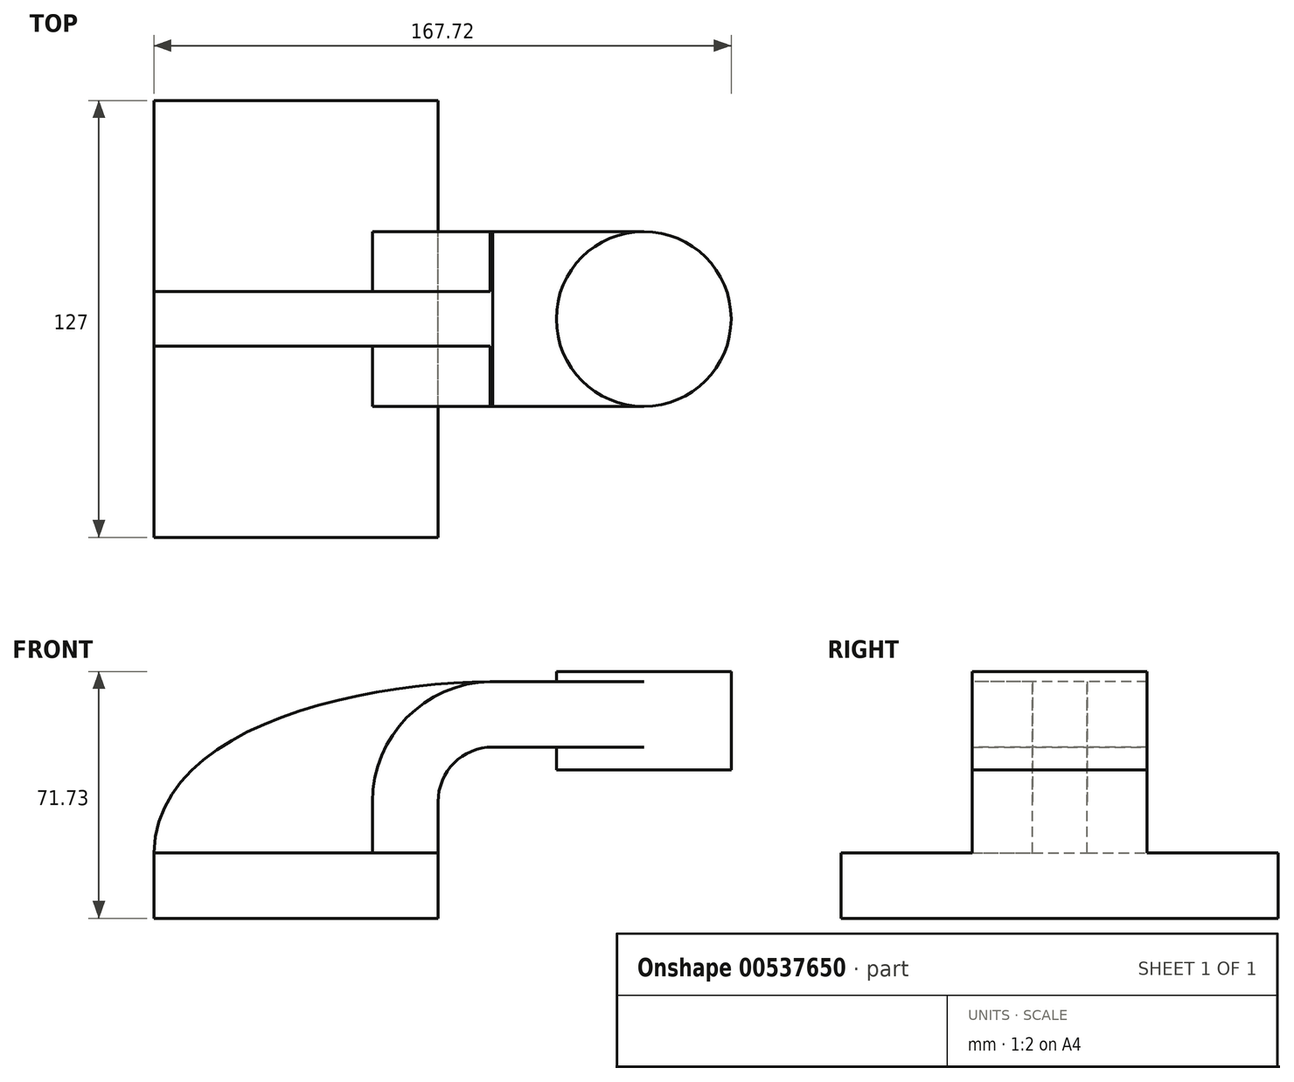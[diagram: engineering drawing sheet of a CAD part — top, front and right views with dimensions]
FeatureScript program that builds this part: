
annotation { "Feature Type Name" : "Feature", "Feature Type Description" : "" }
export const myFeature = defineFeature(function(context is Context, id is Id, definition is map)
    precondition{}
    {
        {
            var Q0;
            Q0=qCreatedBy(makeId("Front.planeOp"),FACE);
            var sketch = newSketch(context, id + "F0", { "sketchPlane" : qUnion([Q0])});
            skLineSegment(sketch, "E0.bottom", {"start": v(-41.28, 9.52) * mm, "end": v(41.28, 9.53) * mm});
            skLineSegment(sketch, "E0.top", {"start": v(-41.27, -9.53) * mm, "end": v(41.28, -9.53) * mm});
            skLineSegment(sketch, "E0.left", {"start": v(-41.27, 9.52) * mm, "end": v(-41.27, -9.53) * mm});
            skLineSegment(sketch, "E0.right", {"start": v(41.28, 9.52) * mm, "end": v(41.28, -9.52) * mm});
            skPoint(sketch, "E0.middle", {"position": v(0, 0) * mm});
            skLineSegment(sketch, "E1.bottom", {"start": v(75.64, 62.2) * mm, "end": v(126.44, 62.2) * mm});
            skLineSegment(sketch, "E1.top", {"start": v(75.64, 33.63) * mm, "end": v(126.44, 33.63) * mm});
            skLineSegment(sketch, "E1.left", {"start": v(75.64, 62.2) * mm, "end": v(75.64, 33.63) * mm});
            skLineSegment(sketch, "E1.right", {"start": v(126.44, 62.2) * mm, "end": v(126.44, 33.63) * mm});
            skPoint(sketch, "E1.middle", {"position": v(101.04, 47.91) * mm});
            skPoint(sketch, "E2.end.orphan", {"position": v(101.04, 40.23) * mm});
            skLineSegment(sketch, "E3", {"start": v(41.28, 9.53) * mm, "end": v(41.28, 24.36) * mm});
            skArc(sketch, "E4", {"start": v(41.28, 24.36) * mm, "mid": v(45.92, 35.58) * mm, "end": v(57.15, 40.23) * mm});
            skLineSegment(sketch, "E5", {"start": v(57.15, 40.23) * mm, "end": v(101.04, 40.23) * mm});
            skLineSegment(sketch, "E6.0", {"start": v(57.15, 59.28) * mm, "end": v(101.04, 59.28) * mm});
            skArc(sketch, "E6.1", {"start": v(22.23, 24.36) * mm, "mid": v(32.45, 49.05) * mm, "end": v(57.15, 59.28) * mm});
            skLineSegment(sketch, "E6.2", {"start": v(22.23, 9.53) * mm, "end": v(22.23, 24.36) * mm});
            skFitSpline(sketch, "E7", {"points": [v(-41.28, 9.52) * mm, v(57.15, 59.28) * mm], "startDerivative": vector(2.01, 110.07) * mm, "endDerivative": vector(117.13, 1) * mm});
            skLineSegment(sketch, "E8", {"start": v(101.04, 62.2) * mm, "end": v(101.04, 33.63) * mm});
            skSolve(sketch);
        }
        {
            var Q0;
            Q0=makeQuery(id+"F0.imprint","IMPRINT",FACE,{"disambiguationData":[TD([[makeQuery(id+"F0.imprint","IMPRINT",EDGE,{"derivedFrom":sQuery(id+"F0.wireOp",EDGE,"E0.top")}),1.0]])]});
            extrude(context, id + "F1", {"entities" : qUnion([Q0]), "endBound" : BoundingType.SYMMETRIC, "depth" : 127 * mm, "offsetDistance" : 25.4 * mm});
        }
        {
            var Q0;
            {var subQ1=sQuery(id+"F0.wireOp",EDGE,"E3");Q0=makeQuery(id+"F0.imprint","IMPRINT",FACE,{"disambiguationData":[TD([[makeQuery(id+"F0.imprint","IMPRINT",EDGE,{"derivedFrom":subQ1}),1.0]])]});}
            var Q1;
            {var subQ0=sQuery(id+"F0.wireOp",EDGE,"E6.0");var subQ1=sQuery(id+"F0.wireOp",EDGE,"E1.left");var subQ2=makeQuery(id+"F0.imprint","INTERSECT",VERTEX,{"derivedFrom":[subQ1,subQ0]});Q1=makeQuery(id+"F0.imprint","IMPRINT",FACE,{"disambiguationData":[TD([[makeQuery(id+"F0.imprint","IMPRINT",EDGE,{"disambiguationData":[TD([[subQ2,-1.0]])],"derivedFrom":subQ1}),1.0]])]});}
            extrude(context, id + "F2", {"entities" : qUnion([Q0, Q1]), "operationType" : NewBodyOperationType.ADD, "endBound" : BoundingType.SYMMETRIC, "depth" : 50.8 * mm, "offsetDistance" : 25.4 * mm});
        }
        {
            var Q0;
            {var subQ3=sQuery(id+"F0.wireOp",EDGE,"E6.2");Q0=makeQuery(id+"F0.imprint","IMPRINT",FACE,{"disambiguationData":[TD([[makeQuery(id+"F0.imprint","IMPRINT",EDGE,{"derivedFrom":subQ3}),1.0]])]});}
            extrude(context, id + "F3", {"entities" : qUnion([Q0]), "operationType" : NewBodyOperationType.ADD, "endBound" : BoundingType.SYMMETRIC, "depth" : 15.88 * mm, "offsetDistance" : 25.4 * mm});
        }
        {
            var Q0;
            {var subQ4=sQuery(id+"F0.wireOp",EDGE,"E1.right");Q0=makeQuery(id+"F0.imprint","IMPRINT",FACE,{"disambiguationData":[TD([[makeQuery(id+"F0.imprint","IMPRINT",EDGE,{"derivedFrom":subQ4}),-1.0]])]});}
            var Q1;
            Q1=sQuery(id+"F0.wireOp",EDGE,"E8");
            revolve(context, id + "F4", {"operationType" : NewBodyOperationType.ADD, "entities" : qUnion([Q0]), "axis" : qUnion([Q1]), "revolveType" : RevolveType.FULL});
        }
    });
